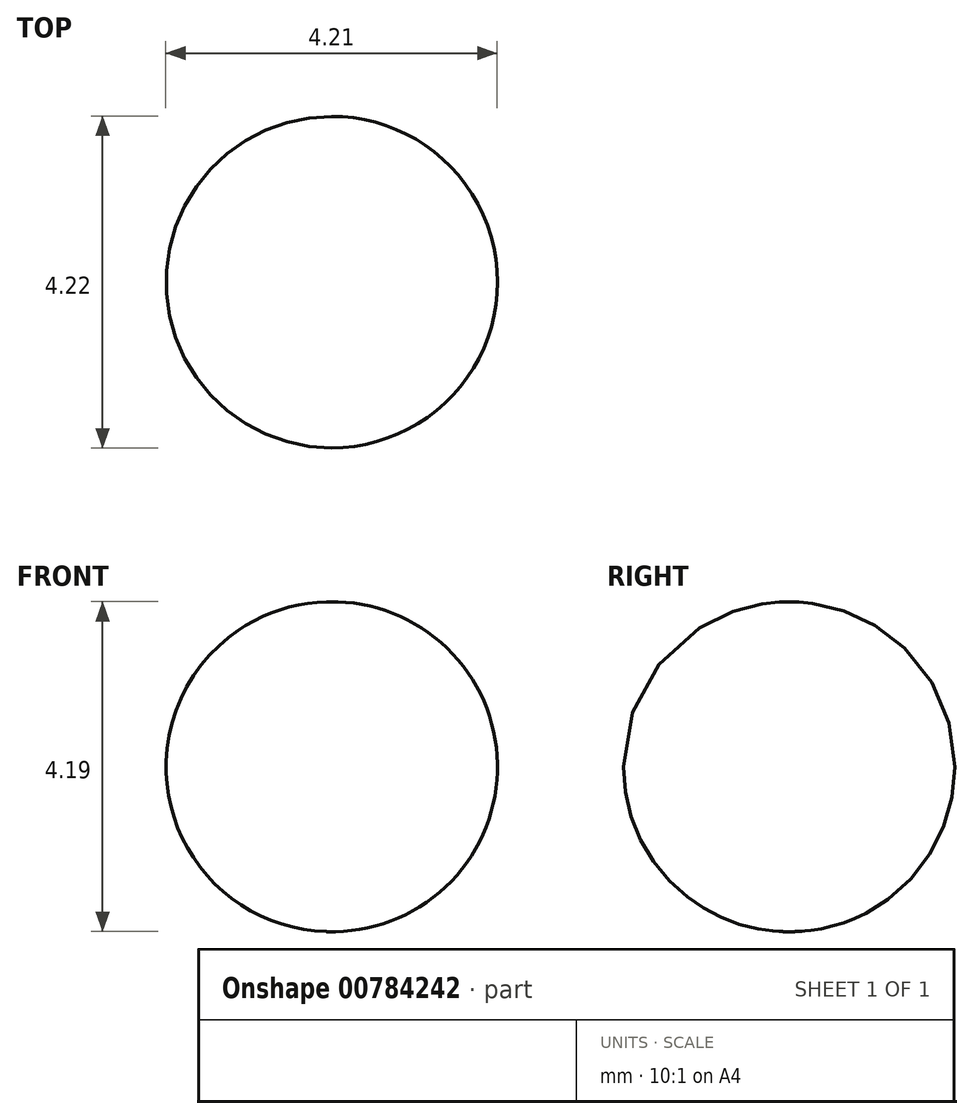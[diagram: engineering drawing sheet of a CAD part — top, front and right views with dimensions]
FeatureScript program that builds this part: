
annotation { "Feature Type Name" : "Feature", "Feature Type Description" : "" }
export const myFeature = defineFeature(function(context is Context, id is Id, definition is map)
    precondition{}
    {
        {
            var Q0;
            Q0=qCreatedBy(makeId("Front.planeOp"),FACE);
            var sketch = newSketch(context, id + "F0", { "sketchPlane" : qUnion([Q0])});
            skArc(sketch, "E0", {"start": v(-6.56, 1.84) * mm, "mid": v(0.01, 8) * mm, "end": v(-6.17, 14.54) * mm});
            skLineSegment(sketch, "E1", {"start": v(-6.17, 14.54) * mm, "end": v(-6.56, 1.84) * mm});
            skSolve(sketch);
        }
        {
            var Q0;
            Q0 = qSketchRegion(id + "F0", true);
            var Q1;
            Q1=sQuery(id+"F0.wireOp",EDGE,"E1");
            revolve(context, id + "F1", {"surfaceOperationType" : NewSurfaceOperationType.NEW, "entities" : qUnion([Q0]), "axis" : qUnion([Q1]), "revolveType" : RevolveType.FULL});
        }
        {
            var Q0;
            Q0=makeQuery(id+"F1.opRevolve","SWEPT_BODY",BODY,{"disambiguationData":[OSD([sQuery(id+"F0.wireOp",EDGE,"E0"),sQuery(id+"F0.wireOp",EDGE,"E1")])]});
            var Q1;
            Q1=qCreatedBy(makeId("Origin.pointOp"),VERTEX);
            transform(context, id + "F2", {"entities" : qUnion([Q0]), "transformType" : TransformType.SCALE_UNIFORMLY, "scale" : .33, "scalePoint" : qUnion([Q1]), "makeCopy" : false});
        }
    });
